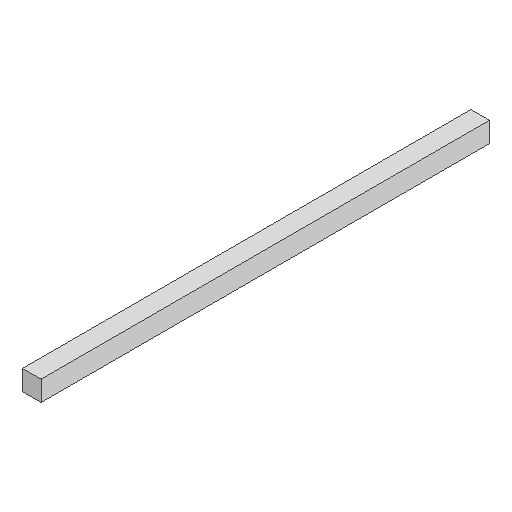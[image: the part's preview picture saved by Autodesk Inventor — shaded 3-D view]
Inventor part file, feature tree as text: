
AUTODESK INVENTOR PART (.ipt)
format: ipt  version: 2024 (Build 280153000, 153)  size: 79,360 bytes
history: native  units: mm
features: other x3, sketch x1
ambient origin geometry x8: Origin, YZ Plane, XZ Plane, XY Plane, X Axis, Y Axis, Z Axis, Center Point
bodies: Solid1 (feature_tree)
feature tree (4):
  other  "pylon.ipt"
  other  "Solid1::pylon.ipt"
  other  "TaggingFeature1"
  sketch  "Sketch1"  dims[d0=10.0mm]
